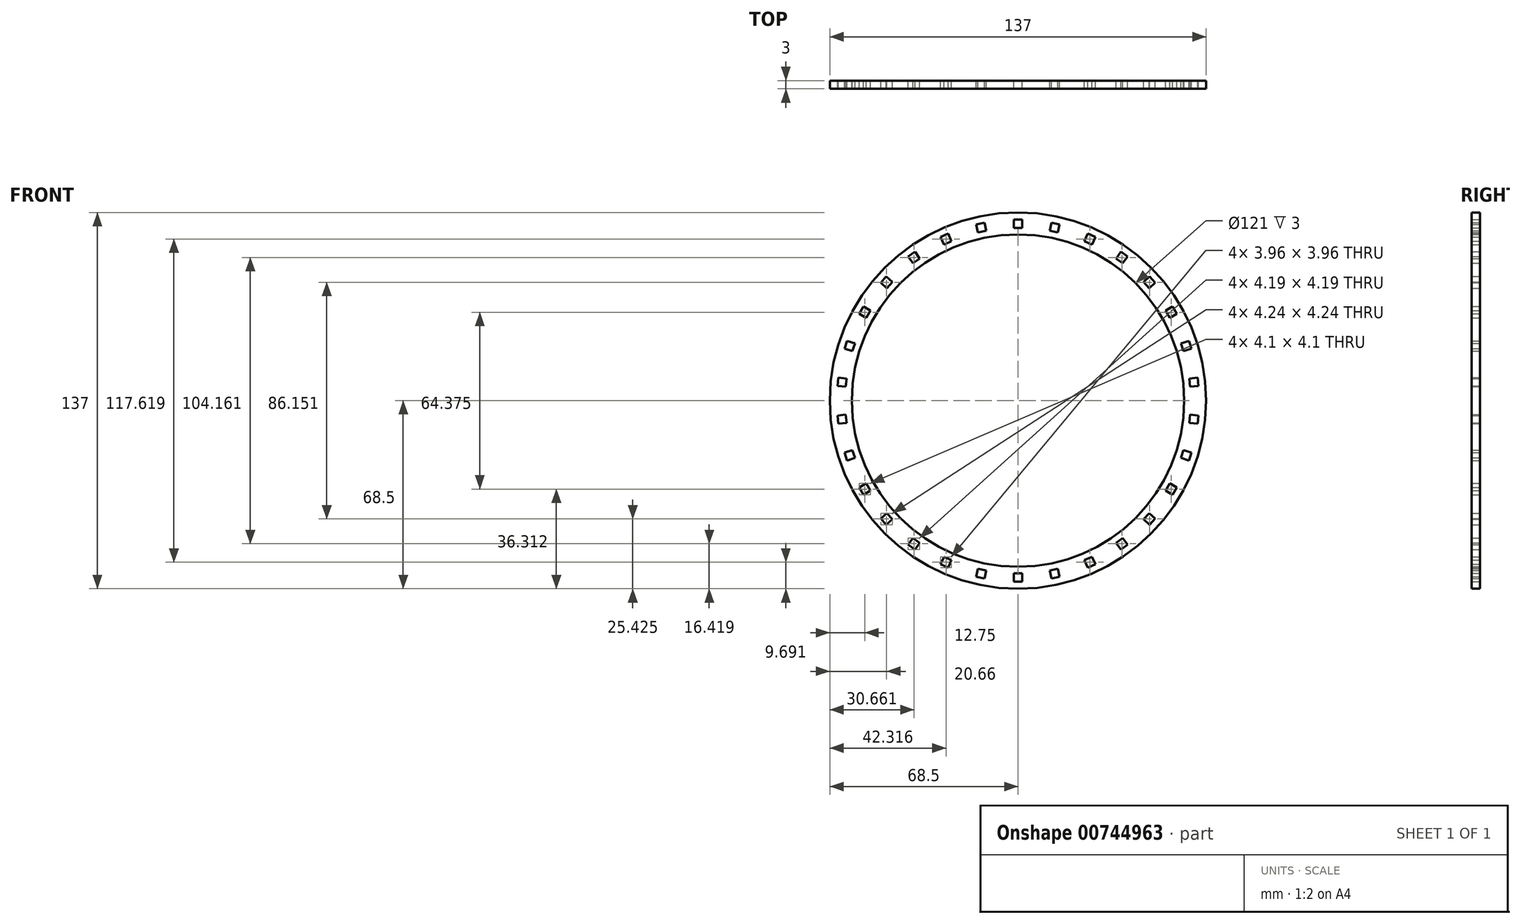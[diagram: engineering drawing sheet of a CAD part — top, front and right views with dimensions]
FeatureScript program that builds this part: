
annotation { "Feature Type Name" : "Feature", "Feature Type Description" : "" }
export const myFeature = defineFeature(function(context is Context, id is Id, definition is map)
    precondition{}
    {
        {
            var Q0;
            Q0=qCreatedBy(makeId("Front.planeOp"),FACE);
            var sketch = newSketch(context, id + "F0", { "sketchPlane" : qUnion([Q0])});
            skCircle(sketch, "E0", {"center": v(0, 0) * mm, "radius": 68.5 * mm});
            skCircle(sketch, "E1", {"center": v(0, 0) * mm, "radius": 60.5 * mm});
            skSolve(sketch);
        }
        {
            var Q0;
            Q0=makeQuery(id+"F0.imprint","IMPRINT",FACE,{"disambiguationData":[TD([[makeQuery(id+"F0.imprint","IMPRINT",EDGE,{"derivedFrom":sQuery(id+"F0.wireOp",EDGE,"E0")}),1.0]])]});
            extrude(context, id + "F1", {"entities" : qUnion([Q0]), "depth" : 3 * mm, "offsetDistance" : 25 * mm});
        }
        {
            var Q0;
            Q0=qCreatedBy(makeId("Front.planeOp"),FACE);
            var sketch = newSketch(context, id + "F2", { "sketchPlane" : qUnion([Q0])});
            skLineSegment(sketch, "E2.bottom", {"start": v(-1.5, 65.88) * mm, "end": v(1.5, 65.88) * mm});
            skLineSegment(sketch, "E2.top", {"start": v(-1.5, 62.88) * mm, "end": v(1.5, 62.88) * mm});
            skLineSegment(sketch, "E2.left", {"start": v(-1.5, 65.88) * mm, "end": v(-1.5, 62.88) * mm});
            skLineSegment(sketch, "E2.right", {"start": v(1.5, 65.88) * mm, "end": v(1.5, 62.88) * mm});
            skLineSegment(sketch, "E3.1.0", {"start": v(-15.16, 64.12) * mm, "end": v(-12.23, 64.75) * mm});
            skLineSegment(sketch, "E3.1.1", {"start": v(-12.23, 64.75) * mm, "end": v(-11.6, 61.81) * mm});
            skLineSegment(sketch, "E3.1.2", {"start": v(-14.54, 61.19) * mm, "end": v(-11.6, 61.81) * mm});
            skLineSegment(sketch, "E3.1.3", {"start": v(-15.16, 64.12) * mm, "end": v(-14.54, 61.19) * mm});
            skLineSegment(sketch, "E3.2.0", {"start": v(-28.16, 59.57) * mm, "end": v(-25.42, 60.79) * mm});
            skLineSegment(sketch, "E3.2.1", {"start": v(-25.42, 60.79) * mm, "end": v(-24.2, 58.05) * mm});
            skLineSegment(sketch, "E3.2.2", {"start": v(-26.94, 56.83) * mm, "end": v(-24.2, 58.05) * mm});
            skLineSegment(sketch, "E3.2.3", {"start": v(-28.16, 59.57) * mm, "end": v(-26.94, 56.83) * mm});
            skPoint(sketch, "E3.center", {"position": v(0, 0) * mm});
            skLineSegment(sketch, "E4.3.3.0", {"start": v(-37.5, 54.18) * mm, "end": v(-35.74, 51.75) * mm});
            skLineSegment(sketch, "E4.6.3.0", {"start": v(-38.17, 49.99) * mm, "end": v(-35.74, 51.75) * mm});
            skLineSegment(sketch, "E4.7.3.0", {"start": v(-39.93, 52.41) * mm, "end": v(-37.5, 54.18) * mm});
            skLineSegment(sketch, "E4.9.3.0", {"start": v(-39.93, 52.41) * mm, "end": v(-38.17, 49.99) * mm});
            skLineSegment(sketch, "E4.3.4.0", {"start": v(-47.95, 45.2) * mm, "end": v(-45.72, 43.19) * mm});
            skLineSegment(sketch, "E4.6.4.0", {"start": v(-47.73, 40.96) * mm, "end": v(-45.72, 43.19) * mm});
            skLineSegment(sketch, "E4.7.4.0", {"start": v(-49.96, 42.96) * mm, "end": v(-47.95, 45.2) * mm});
            skLineSegment(sketch, "E4.9.4.0", {"start": v(-49.96, 42.96) * mm, "end": v(-47.73, 40.96) * mm});
            skLineSegment(sketch, "E4.3.5.0", {"start": v(-56.3, 34.24) * mm, "end": v(-53.7, 32.74) * mm});
            skLineSegment(sketch, "E4.6.5.0", {"start": v(-55.2, 30.14) * mm, "end": v(-53.7, 32.74) * mm});
            skLineSegment(sketch, "E4.7.5.0", {"start": v(-57.8, 31.64) * mm, "end": v(-56.3, 34.24) * mm});
            skLineSegment(sketch, "E4.9.5.0", {"start": v(-57.8, 31.64) * mm, "end": v(-55.2, 30.14) * mm});
            skLineSegment(sketch, "E4.3.6.0", {"start": v(-62.19, 21.78) * mm, "end": v(-59.33, 20.86) * mm});
            skLineSegment(sketch, "E4.6.6.0", {"start": v(-60.26, 18) * mm, "end": v(-59.33, 20.86) * mm});
            skLineSegment(sketch, "E4.7.6.0", {"start": v(-63.11, 18.93) * mm, "end": v(-62.19, 21.78) * mm});
            skLineSegment(sketch, "E4.9.6.0", {"start": v(-63.11, 18.93) * mm, "end": v(-60.26, 18) * mm});
            skLineSegment(sketch, "E4.3.7.0", {"start": v(-65.36, 8.38) * mm, "end": v(-62.37, 8.06) * mm});
            skLineSegment(sketch, "E4.6.7.0", {"start": v(-62.69, 5.08) * mm, "end": v(-62.37, 8.06) * mm});
            skLineSegment(sketch, "E4.7.7.0", {"start": v(-65.67, 5.4) * mm, "end": v(-65.36, 8.38) * mm});
            skLineSegment(sketch, "E4.9.7.0", {"start": v(-65.67, 5.4) * mm, "end": v(-62.69, 5.08) * mm});
            skLineSegment(sketch, "E4.3.8.0", {"start": v(-65.67, -5.4) * mm, "end": v(-62.69, -5.08) * mm});
            skLineSegment(sketch, "E4.6.8.0", {"start": v(-62.37, -8.06) * mm, "end": v(-62.69, -5.08) * mm});
            skLineSegment(sketch, "E4.7.8.0", {"start": v(-65.36, -8.38) * mm, "end": v(-65.67, -5.4) * mm});
            skLineSegment(sketch, "E4.9.8.0", {"start": v(-65.36, -8.38) * mm, "end": v(-62.37, -8.06) * mm});
            skLineSegment(sketch, "E4.3.9.0", {"start": v(-63.11, -18.93) * mm, "end": v(-60.26, -18) * mm});
            skLineSegment(sketch, "E4.6.9.0", {"start": v(-59.33, -20.86) * mm, "end": v(-60.26, -18) * mm});
            skLineSegment(sketch, "E4.7.9.0", {"start": v(-62.19, -21.78) * mm, "end": v(-63.11, -18.93) * mm});
            skLineSegment(sketch, "E4.9.9.0", {"start": v(-62.19, -21.78) * mm, "end": v(-59.33, -20.86) * mm});
            skLineSegment(sketch, "E4.3.10.0", {"start": v(-57.8, -31.64) * mm, "end": v(-55.2, -30.14) * mm});
            skLineSegment(sketch, "E4.6.10.0", {"start": v(-53.7, -32.74) * mm, "end": v(-55.2, -30.14) * mm});
            skLineSegment(sketch, "E4.7.10.0", {"start": v(-56.3, -34.24) * mm, "end": v(-57.8, -31.64) * mm});
            skLineSegment(sketch, "E4.9.10.0", {"start": v(-56.3, -34.24) * mm, "end": v(-53.7, -32.74) * mm});
            skLineSegment(sketch, "E4.3.11.0", {"start": v(-49.96, -42.96) * mm, "end": v(-47.73, -40.96) * mm});
            skLineSegment(sketch, "E4.6.11.0", {"start": v(-45.72, -43.19) * mm, "end": v(-47.73, -40.96) * mm});
            skLineSegment(sketch, "E4.7.11.0", {"start": v(-47.95, -45.2) * mm, "end": v(-49.96, -42.96) * mm});
            skLineSegment(sketch, "E4.9.11.0", {"start": v(-47.95, -45.2) * mm, "end": v(-45.72, -43.19) * mm});
            skLineSegment(sketch, "E4.3.12.0", {"start": v(-39.93, -52.41) * mm, "end": v(-38.17, -49.99) * mm});
            skLineSegment(sketch, "E4.6.12.0", {"start": v(-35.74, -51.75) * mm, "end": v(-38.17, -49.99) * mm});
            skLineSegment(sketch, "E4.7.12.0", {"start": v(-37.5, -54.18) * mm, "end": v(-39.93, -52.41) * mm});
            skLineSegment(sketch, "E4.9.12.0", {"start": v(-37.5, -54.18) * mm, "end": v(-35.74, -51.75) * mm});
            skLineSegment(sketch, "E4.3.13.0", {"start": v(-28.16, -59.57) * mm, "end": v(-26.94, -56.83) * mm});
            skLineSegment(sketch, "E4.6.13.0", {"start": v(-24.2, -58.05) * mm, "end": v(-26.94, -56.83) * mm});
            skLineSegment(sketch, "E4.7.13.0", {"start": v(-25.42, -60.79) * mm, "end": v(-28.16, -59.57) * mm});
            skLineSegment(sketch, "E4.9.13.0", {"start": v(-25.42, -60.79) * mm, "end": v(-24.2, -58.05) * mm});
            skLineSegment(sketch, "E4.3.14.0", {"start": v(-15.16, -64.12) * mm, "end": v(-14.54, -61.19) * mm});
            skLineSegment(sketch, "E4.6.14.0", {"start": v(-11.6, -61.81) * mm, "end": v(-14.54, -61.19) * mm});
            skLineSegment(sketch, "E4.7.14.0", {"start": v(-12.23, -64.75) * mm, "end": v(-15.16, -64.12) * mm});
            skLineSegment(sketch, "E4.9.14.0", {"start": v(-12.23, -64.75) * mm, "end": v(-11.6, -61.81) * mm});
            skLineSegment(sketch, "E4.3.15.0", {"start": v(-1.5, -65.88) * mm, "end": v(-1.5, -62.88) * mm});
            skLineSegment(sketch, "E4.6.15.0", {"start": v(1.5, -62.88) * mm, "end": v(-1.5, -62.88) * mm});
            skLineSegment(sketch, "E4.7.15.0", {"start": v(1.5, -65.88) * mm, "end": v(-1.5, -65.88) * mm});
            skLineSegment(sketch, "E4.9.15.0", {"start": v(1.5, -65.88) * mm, "end": v(1.5, -62.88) * mm});
            skLineSegment(sketch, "E4.3.16.0", {"start": v(12.23, -64.75) * mm, "end": v(11.6, -61.81) * mm});
            skLineSegment(sketch, "E4.6.16.0", {"start": v(14.54, -61.19) * mm, "end": v(11.6, -61.81) * mm});
            skLineSegment(sketch, "E4.7.16.0", {"start": v(15.16, -64.12) * mm, "end": v(12.23, -64.75) * mm});
            skLineSegment(sketch, "E4.9.16.0", {"start": v(15.16, -64.12) * mm, "end": v(14.54, -61.19) * mm});
            skLineSegment(sketch, "E4.3.17.0", {"start": v(25.42, -60.79) * mm, "end": v(24.2, -58.05) * mm});
            skLineSegment(sketch, "E4.6.17.0", {"start": v(26.94, -56.83) * mm, "end": v(24.2, -58.05) * mm});
            skLineSegment(sketch, "E4.7.17.0", {"start": v(28.16, -59.57) * mm, "end": v(25.42, -60.79) * mm});
            skLineSegment(sketch, "E4.9.17.0", {"start": v(28.16, -59.57) * mm, "end": v(26.94, -56.83) * mm});
            skLineSegment(sketch, "E4.3.18.0", {"start": v(37.5, -54.18) * mm, "end": v(35.74, -51.75) * mm});
            skLineSegment(sketch, "E4.6.18.0", {"start": v(38.17, -49.99) * mm, "end": v(35.74, -51.75) * mm});
            skLineSegment(sketch, "E4.7.18.0", {"start": v(39.93, -52.41) * mm, "end": v(37.5, -54.18) * mm});
            skLineSegment(sketch, "E4.9.18.0", {"start": v(39.93, -52.41) * mm, "end": v(38.17, -49.99) * mm});
            skLineSegment(sketch, "E4.3.19.0", {"start": v(47.95, -45.2) * mm, "end": v(45.72, -43.19) * mm});
            skLineSegment(sketch, "E4.6.19.0", {"start": v(47.73, -40.96) * mm, "end": v(45.72, -43.19) * mm});
            skLineSegment(sketch, "E4.7.19.0", {"start": v(49.96, -42.96) * mm, "end": v(47.95, -45.2) * mm});
            skLineSegment(sketch, "E4.9.19.0", {"start": v(49.96, -42.96) * mm, "end": v(47.73, -40.96) * mm});
            skLineSegment(sketch, "E4.3.20.0", {"start": v(56.3, -34.24) * mm, "end": v(53.7, -32.74) * mm});
            skLineSegment(sketch, "E4.6.20.0", {"start": v(55.2, -30.14) * mm, "end": v(53.7, -32.74) * mm});
            skLineSegment(sketch, "E4.7.20.0", {"start": v(57.8, -31.64) * mm, "end": v(56.3, -34.24) * mm});
            skLineSegment(sketch, "E4.9.20.0", {"start": v(57.8, -31.64) * mm, "end": v(55.2, -30.14) * mm});
            skLineSegment(sketch, "E4.3.21.0", {"start": v(62.19, -21.78) * mm, "end": v(59.33, -20.86) * mm});
            skLineSegment(sketch, "E4.6.21.0", {"start": v(60.26, -18) * mm, "end": v(59.33, -20.86) * mm});
            skLineSegment(sketch, "E4.7.21.0", {"start": v(63.11, -18.93) * mm, "end": v(62.19, -21.78) * mm});
            skLineSegment(sketch, "E4.9.21.0", {"start": v(63.11, -18.93) * mm, "end": v(60.26, -18) * mm});
            skLineSegment(sketch, "E4.3.22.0", {"start": v(65.36, -8.38) * mm, "end": v(62.37, -8.06) * mm});
            skLineSegment(sketch, "E4.6.22.0", {"start": v(62.69, -5.08) * mm, "end": v(62.37, -8.06) * mm});
            skLineSegment(sketch, "E4.7.22.0", {"start": v(65.67, -5.4) * mm, "end": v(65.36, -8.38) * mm});
            skLineSegment(sketch, "E4.9.22.0", {"start": v(65.67, -5.4) * mm, "end": v(62.69, -5.08) * mm});
            skLineSegment(sketch, "E4.3.23.0", {"start": v(65.67, 5.4) * mm, "end": v(62.69, 5.08) * mm});
            skLineSegment(sketch, "E4.6.23.0", {"start": v(62.37, 8.06) * mm, "end": v(62.69, 5.08) * mm});
            skLineSegment(sketch, "E4.7.23.0", {"start": v(65.36, 8.38) * mm, "end": v(65.67, 5.4) * mm});
            skLineSegment(sketch, "E4.9.23.0", {"start": v(65.36, 8.38) * mm, "end": v(62.37, 8.06) * mm});
            skLineSegment(sketch, "E4.3.24.0", {"start": v(63.11, 18.93) * mm, "end": v(60.26, 18) * mm});
            skLineSegment(sketch, "E4.6.24.0", {"start": v(59.33, 20.86) * mm, "end": v(60.26, 18) * mm});
            skLineSegment(sketch, "E4.7.24.0", {"start": v(62.19, 21.78) * mm, "end": v(63.11, 18.93) * mm});
            skLineSegment(sketch, "E4.9.24.0", {"start": v(62.19, 21.78) * mm, "end": v(59.33, 20.86) * mm});
            skLineSegment(sketch, "E4.3.25.0", {"start": v(57.8, 31.64) * mm, "end": v(55.2, 30.14) * mm});
            skLineSegment(sketch, "E4.6.25.0", {"start": v(53.7, 32.74) * mm, "end": v(55.2, 30.14) * mm});
            skLineSegment(sketch, "E4.7.25.0", {"start": v(56.3, 34.24) * mm, "end": v(57.8, 31.64) * mm});
            skLineSegment(sketch, "E4.9.25.0", {"start": v(56.3, 34.24) * mm, "end": v(53.7, 32.74) * mm});
            skLineSegment(sketch, "E4.3.26.0", {"start": v(49.96, 42.96) * mm, "end": v(47.73, 40.96) * mm});
            skLineSegment(sketch, "E4.6.26.0", {"start": v(45.72, 43.19) * mm, "end": v(47.73, 40.96) * mm});
            skLineSegment(sketch, "E4.7.26.0", {"start": v(47.95, 45.2) * mm, "end": v(49.96, 42.96) * mm});
            skLineSegment(sketch, "E4.9.26.0", {"start": v(47.95, 45.2) * mm, "end": v(45.72, 43.19) * mm});
            skLineSegment(sketch, "E4.3.27.0", {"start": v(39.93, 52.41) * mm, "end": v(38.17, 49.99) * mm});
            skLineSegment(sketch, "E4.6.27.0", {"start": v(35.74, 51.75) * mm, "end": v(38.17, 49.99) * mm});
            skLineSegment(sketch, "E4.7.27.0", {"start": v(37.5, 54.18) * mm, "end": v(39.93, 52.41) * mm});
            skLineSegment(sketch, "E4.9.27.0", {"start": v(37.5, 54.18) * mm, "end": v(35.74, 51.75) * mm});
            skLineSegment(sketch, "E4.3.28.0", {"start": v(28.16, 59.57) * mm, "end": v(26.94, 56.83) * mm});
            skLineSegment(sketch, "E4.6.28.0", {"start": v(24.2, 58.05) * mm, "end": v(26.94, 56.83) * mm});
            skLineSegment(sketch, "E4.7.28.0", {"start": v(25.42, 60.79) * mm, "end": v(28.16, 59.57) * mm});
            skLineSegment(sketch, "E4.9.28.0", {"start": v(25.42, 60.79) * mm, "end": v(24.2, 58.05) * mm});
            skLineSegment(sketch, "E4.3.29.0", {"start": v(15.16, 64.12) * mm, "end": v(14.54, 61.19) * mm});
            skLineSegment(sketch, "E4.6.29.0", {"start": v(11.6, 61.81) * mm, "end": v(14.54, 61.19) * mm});
            skLineSegment(sketch, "E4.7.29.0", {"start": v(12.23, 64.75) * mm, "end": v(15.16, 64.12) * mm});
            skLineSegment(sketch, "E4.9.29.0", {"start": v(12.23, 64.75) * mm, "end": v(11.6, 61.81) * mm});
            skSolve(sketch);
        }
        {
            var Q0;
            Q0 = qSketchRegion(id + "F2", true);
            extrude(context, id + "F3", {"entities" : qUnion([Q0]), "operationType" : NewBodyOperationType.REMOVE, "depth" : 3 * mm, "offsetDistance" : 25 * mm});
        }
    });
